# Revit family: Б4958_RV17_LOD400 (05.11.23)
name_source: partatom
category: Электрооборудование
revit_build: Autodesk Revit 2017 (Build: 20170118_1100(x64)
units: mm (PartAtom-declared; Revit-internal decimal feet)

## family parameters
Всегда вертикально = Нет
Конфигурация панели = Два столбца, слева направо
На основе рабочей плоскости = Да
Общий = Нет
При загрузке вырезать с полостями = Нет
Размер круглого соединителя = Использовать диаметр
Тип детали = Щит
Точка расчета площади = Нет

## types (1)
- Б4958_Инжектор PoE
    ADSK_URL страницы изделия = https://stilsoft.ru
    ADSK_Единица измерения = шт.
    ADSK_Завод-изготовитель = ООО «Основа Безопасности»
    ADSK_Количество = 1
    ADSK_Марка = СТВФ.426471.092
    ADSK_Масса = 2.6
    ADSK_Наименование = Инжектор РоЕ Б4958

 
Инжектор РоЕ Б4958

Инжектор РоЕ Б4958
    ADSK_Размер_Высота = 45 мм
    ADSK_Размер_Глубина = 187 мм
    ADSK_Размер_Длина = 313 мм
    d_короба = 20 мм
    Время непрерывной работы = круглосуточно
    Выходное напряжение постоянного тока, В = 48 Passive РоЕ
    Диапазон рабочих температур, °С = от – 40 до + 50
    Количество портов LAN и PoE, шт. = 8
    Максимальная мощность подключаемого устройства по РоЕ на один порт, не более, Вт = 25
    Мощность = 25
    Напряжение = 220
    Отметка по умолчанию = 1219 мм
    Потребляемый ток, не более, А = 2 А
    Расстояние передачи, до, м = 100
    Стандарт интерфейса связи = 10/100 Base-T Ethernet
    Суммарная мощность подключаемых устройств по РоЕ, Вт = 200
